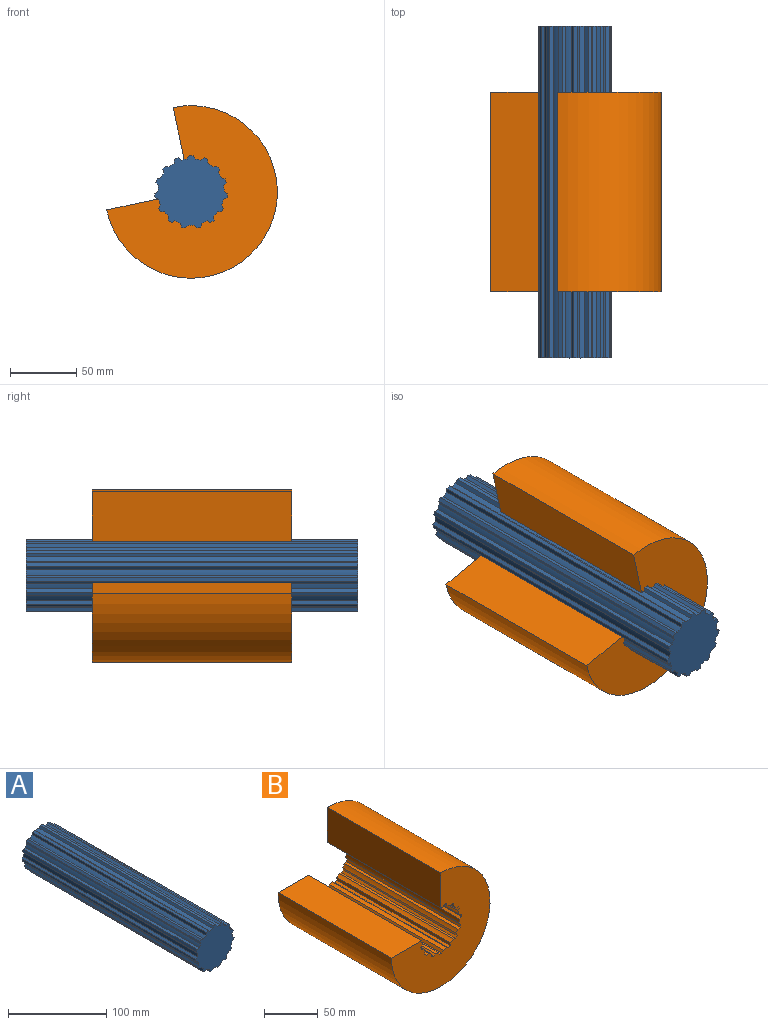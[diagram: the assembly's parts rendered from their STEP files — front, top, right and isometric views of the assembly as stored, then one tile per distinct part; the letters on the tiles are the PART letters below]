
ASSEMBLY  parts=2 mates=1
PART A: 62 faces, bbox 54.8x250x54.5 mm
  f0: cylinder r=25mm len=250mm, axis (0,1,0), area 1114.4mm2, adj f15,f16,f37,f40
  f1: cylinder r=25mm len=250mm, axis (0,1,0), area 1114.4mm2, adj f15,f16,f34,f36
  f2: cylinder r=25mm len=250mm, axis (0,1,0), area 1114.4mm2, adj f15,f16,f31,f33
  f3: cylinder r=25mm len=250mm, axis (0,1,0), area 1114.4mm2, adj f15,f16,f28,f30
  f4: cylinder r=25mm len=250mm, axis (0,1,0), area 1114.4mm2, adj f15,f16,f25,f27
  f5: cylinder r=25mm len=250mm, axis (0,1,0), area 1114.4mm2, adj f15,f16,f22,f24
  f6: cylinder r=25mm len=250mm, axis (0,1,0), area 1114.4mm2, adj f15,f16,f19,f21
  f7: cylinder r=25mm len=250mm, axis (0,1,0), area 1114.4mm2, adj f15,f16,f18,f59
  f8: cylinder r=25mm len=250mm, axis (0,1,0), area 1114.4mm2, adj f15,f16,f58,f61
  f9: cylinder r=25mm len=250mm, axis (0,1,0), area 1114.4mm2, adj f15,f16,f55,f57
  f10: cylinder r=25mm len=250mm, axis (0,1,0), area 1114.4mm2, adj f15,f16,f52,f54
  f11: cylinder r=25mm len=250mm, axis (0,1,0), area 1114.4mm2, adj f15,f16,f49,f51
  f12: cylinder r=25mm len=250mm, axis (0,1,0), area 1114.4mm2, adj f15,f16,f46,f48
  f13: cylinder r=25mm len=250mm, axis (0,1,0), area 1114.4mm2, adj f15,f16,f43,f45
  f14: cylinder r=25mm len=250mm, axis (0,1,0), area 1114.4mm2, adj f15,f16,f39,f42
  f15: plane 54.85x54.55mm, normal (0,-1,0), area 2128mm2, adj f0,f1,f2,f3,f4,f5,f6,f7
  f16: plane 54.85x54.55mm, normal (0,1,0), area 2128mm2, adj f0,f1,f2,f3,f4,f5,f6,f7
  f17: plane 250x2.93mm, normal (-0.21,0,-0.98), area 750mm2, adj f15,f16,f18,f19
  f18: plane 250x2.23mm, normal (0.74,0,-0.67), area 750mm2, adj f7,f15,f16,f17
  f19: plane 250x2.85mm, normal (-0.95,0,-0.31), area 750mm2, adj f6,f15,f16,f17
  f20: plane 250x2.43mm, normal (-0.59,0,-0.81), area 750mm2, adj f15,f16,f21,f22
  f21: plane 250x2.74mm, normal (0.41,0,-0.91), area 750mm2, adj f6,f15,f16,f20
  f22: plane 250x2.98mm, normal (-0.99,0,0.1), area 750mm2, adj f5,f15,f16,f20
  f23: plane 250x2.6mm, normal (-0.87,0,-0.5), area 750mm2, adj f15,f16,f24,f25
  f24: plane 250x3mm, normal (0,0,-1), area 750mm2, adj f5,f15,f16,f23
  f25: plane 250x2.6mm, normal (-0.87,0,0.5), area 750mm2, adj f4,f15,f16,f23
  f26: plane 250x2.98mm, normal (-0.99,0,-0.1), area 750mm2, adj f15,f16,f27,f28
  f27: plane 250x2.74mm, normal (-0.41,0,-0.91), area 750mm2, adj f4,f15,f16,f26
  f28: plane 250x2.43mm, normal (-0.59,0,0.81), area 750mm2, adj f3,f15,f16,f26
  f29: plane 250x2.85mm, normal (-0.95,0,0.31), area 750mm2, adj f15,f16,f30,f31
  f30: plane 250x2.23mm, normal (-0.74,0,-0.67), area 750mm2, adj f3,f15,f16,f29
  f31: plane 250x2.93mm, normal (-0.21,0,0.98), area 750mm2, adj f2,f15,f16,f29
  f32: plane 250x2.23mm, normal (-0.74,0,0.67), area 750mm2, adj f15,f16,f33,f34
  f33: plane 250x2.85mm, normal (-0.95,0,-0.31), area 750mm2, adj f2,f15,f16,f32
  f34: plane 250x2.93mm, normal (0.21,0,0.98), area 750mm2, adj f1,f15,f16,f32
  f35: plane 250x2.74mm, normal (-0.41,0,0.91), area 750mm2, adj f15,f16,f36,f37
  f36: plane 250x2.98mm, normal (-0.99,0,0.1), area 750mm2, adj f1,f15,f16,f35
  f37: plane 250x2.43mm, normal (0.59,0,0.81), area 750mm2, adj f0,f15,f16,f35
  f38: plane 250x3mm, normal (0,0,1), area 750mm2, adj f15,f16,f39,f40
  f39: plane 250x2.6mm, normal (0.87,0,0.5), area 750mm2, adj f14,f15,f16,f38
  f40: plane 250x2.6mm, normal (-0.87,0,0.5), area 750mm2, adj f0,f15,f16,f38
  f41: plane 250x2.74mm, normal (0.41,0,0.91), area 750mm2, adj f15,f16,f42,f43
  f42: plane 250x2.43mm, normal (-0.59,0,0.81), area 750mm2, adj f14,f15,f16,f41
  f43: plane 250x2.98mm, normal (0.99,0,0.1), area 750mm2, adj f13,f15,f16,f41
  f44: plane 250x2.23mm, normal (0.74,0,0.67), area 750mm2, adj f15,f16,f45,f46
  f45: plane 250x2.93mm, normal (-0.21,0,0.98), area 750mm2, adj f13,f15,f16,f44
  f46: plane 250x2.85mm, normal (0.95,0,-0.31), area 750mm2, adj f12,f15,f16,f44
  f47: plane 250x2.85mm, normal (0.95,0,0.31), area 750mm2, adj f15,f16,f48,f49
  f48: plane 250x2.93mm, normal (0.21,0,0.98), area 750mm2, adj f12,f15,f16,f47
  f49: plane 250x2.23mm, normal (0.74,0,-0.67), area 750mm2, adj f11,f15,f16,f47
  f50: plane 250x2.98mm, normal (0.99,0,-0.1), area 750mm2, adj f15,f16,f51,f52
  f51: plane 250x2.43mm, normal (0.59,0,0.81), area 750mm2, adj f11,f15,f16,f50
  f52: plane 250x2.74mm, normal (0.41,0,-0.91), area 750mm2, adj f10,f15,f16,f50
  f53: plane 250x2.6mm, normal (0.87,0,-0.5), area 750mm2, adj f15,f16,f54,f55
  f54: plane 250x2.6mm, normal (0.87,0,0.5), area 750mm2, adj f10,f15,f16,f53
  f55: plane 250x3mm, normal (0,0,-1), area 750mm2, adj f9,f15,f16,f53
  f56: plane 250x2.43mm, normal (0.59,0,-0.81), area 750mm2, adj f15,f16,f57,f58
  f57: plane 250x2.98mm, normal (0.99,0,0.1), area 750mm2, adj f9,f15,f16,f56
  f58: plane 250x2.74mm, normal (-0.41,0,-0.91), area 750mm2, adj f8,f15,f16,f56
  f59: plane 250x2.23mm, normal (-0.74,0,-0.67), area 750mm2, adj f7,f15,f16,f60
  f60: plane 250x2.93mm, normal (0.21,0,-0.98), area 750mm2, adj f15,f16,f59,f61
  f61: plane 250x2.85mm, normal (0.95,0,-0.31), area 750mm2, adj f8,f15,f16,f60
PART B: 50 faces, bbox 130x150x130 mm
  f0: cylinder r=25mm len=150mm, axis (0,-1,0), area 727mm2, adj f11,f12,f15,f47
  f1: cylinder r=25mm len=150mm, axis (0,-1,0), area 668.6mm2, adj f11,f12,f43,f44
  f2: cylinder r=25mm len=150mm, axis (0,-1,0), area 668.6mm2, adj f11,f12,f40,f41
  f3: cylinder r=25mm len=150mm, axis (0,-1,0), area 668.6mm2, adj f11,f12,f37,f38
  f4: cylinder r=25mm len=150mm, axis (0,-1,0), area 668.6mm2, adj f11,f12,f34,f35
  f5: cylinder r=25mm len=150mm, axis (0,-1,0), area 668.6mm2, adj f11,f12,f31,f32
  f6: cylinder r=25mm len=150mm, axis (0,-1,0), area 668.6mm2, adj f11,f12,f28,f29
  f7: cylinder r=25mm len=150mm, axis (0,-1,0), area 668.6mm2, adj f11,f12,f19,f26
  f8: cylinder r=25mm len=150mm, axis (0,-1,0), area 668.6mm2, adj f11,f12,f23,f49
  f9: cylinder r=25mm len=150mm, axis (0,-1,0), area 668.6mm2, adj f11,f12,f20,f25
  f10: cylinder r=25mm len=150mm, axis (0,-1,0), area 668.6mm2, adj f11,f12,f17,f22
  f11: plane 130x130mm, normal (0,-1,0), area 8361.6mm2, adj f0,f1,f2,f3,f4,f5,f6,f7
  f12: plane 130x130mm, normal (0,1,0), area 8361.6mm2, adj f0,f1,f2,f3,f4,f5,f6,f7
  f13: cylinder r=65mm len=150mm, axis (0,-1,0), area 45945.8mm2, adj f11,f12,f15,f16
  f14: cylinder r=25mm len=150mm, axis (0,-1,0), area 334.3mm2, adj f11,f12,f16,f46
  f15: plane 150x40mm, normal (0,0,1), area 6000mm2, adj f0,f11,f12,f13
  f16: plane 150x40mm, normal (-1,0,0), area 6000mm2, adj f11,f12,f13,f14
  f17: plane 150x2.6mm, normal (0.87,0,0.5), area 450mm2, adj f10,f11,f12,f18
  f18: plane 150x3mm, normal (0,0,1), area 450mm2, adj f11,f12,f17,f19
  f19: plane 150x2.6mm, normal (-0.87,0,0.5), area 450mm2, adj f7,f11,f12,f18
  f20: plane 150x2.98mm, normal (0.99,0,0.1), area 450mm2, adj f9,f11,f12,f21
  f21: plane 150x2.74mm, normal (0.41,0,0.91), area 450mm2, adj f11,f12,f20,f22
  f22: plane 150x2.43mm, normal (-0.59,0,0.81), area 450mm2, adj f10,f11,f12,f21
  f23: plane 150x2.85mm, normal (0.95,0,-0.31), area 450mm2, adj f8,f11,f12,f24
  f24: plane 150x2.23mm, normal (0.74,0,0.67), area 450mm2, adj f11,f12,f23,f25
  f25: plane 150x2.93mm, normal (-0.21,0,0.98), area 450mm2, adj f9,f11,f12,f24
  f26: plane 150x2.43mm, normal (0.59,0,0.81), area 450mm2, adj f7,f11,f12,f27
  f27: plane 150x2.74mm, normal (-0.41,0,0.91), area 450mm2, adj f11,f12,f26,f28
  f28: plane 150x2.98mm, normal (-0.99,0,0.1), area 450mm2, adj f6,f11,f12,f27
  f29: plane 150x2.93mm, normal (0.21,0,0.98), area 450mm2, adj f6,f11,f12,f30
  f30: plane 150x2.23mm, normal (-0.74,0,0.67), area 450mm2, adj f11,f12,f29,f31
  f31: plane 150x2.85mm, normal (-0.95,0,-0.31), area 450mm2, adj f5,f11,f12,f30
  f32: plane 150x2.93mm, normal (-0.21,0,0.98), area 450mm2, adj f5,f11,f12,f33
  f33: plane 150x2.85mm, normal (-0.95,0,0.31), area 450mm2, adj f11,f12,f32,f34
  f34: plane 150x2.23mm, normal (-0.74,0,-0.67), area 450mm2, adj f4,f11,f12,f33
  f35: plane 150x2.43mm, normal (-0.59,0,0.81), area 450mm2, adj f4,f11,f12,f36
  f36: plane 150x2.98mm, normal (-0.99,0,-0.1), area 450mm2, adj f11,f12,f35,f37
  f37: plane 150x2.74mm, normal (-0.41,0,-0.91), area 450mm2, adj f3,f11,f12,f36
  f38: plane 150x2.6mm, normal (-0.87,0,0.5), area 450mm2, adj f3,f11,f12,f39
  f39: plane 150x2.6mm, normal (-0.87,0,-0.5), area 450mm2, adj f11,f12,f38,f40
  f40: plane 150x3mm, normal (0,0,-1), area 450mm2, adj f2,f11,f12,f39
  f41: plane 150x2.98mm, normal (-0.99,0,0.1), area 450mm2, adj f2,f11,f12,f42
  f42: plane 150x2.43mm, normal (-0.59,0,-0.81), area 450mm2, adj f11,f12,f41,f43
  f43: plane 150x2.74mm, normal (0.41,0,-0.91), area 450mm2, adj f1,f11,f12,f42
  f44: plane 150x2.85mm, normal (-0.95,0,-0.31), area 450mm2, adj f1,f11,f12,f45
  f45: plane 150x2.93mm, normal (-0.21,0,-0.98), area 450mm2, adj f11,f12,f44,f46
  f46: plane 150x2.23mm, normal (0.74,0,-0.67), area 450mm2, adj f11,f12,f14,f45
  f47: plane 150x2.23mm, normal (0.74,0,-0.67), area 450mm2, adj f0,f11,f12,f48
  f48: plane 150x2.85mm, normal (0.95,0,0.31), area 450mm2, adj f11,f12,f47,f49
  f49: plane 150x2.93mm, normal (0.21,0,0.98), area 450mm2, adj f8,f11,f12,f48
PLACE A rot(axis=(0,-1,0),0deg) t=(-164.24,107.25,15.25)mm
PLACE B rot(axis=(0,-1,0),12deg) t=(-164.24,-17.75,15.25)mm fixed
MATE fastened A.f47 <-> B.f36  axis (0.95,0,0.31) through (-138.16,-17.75,23.72)mm
